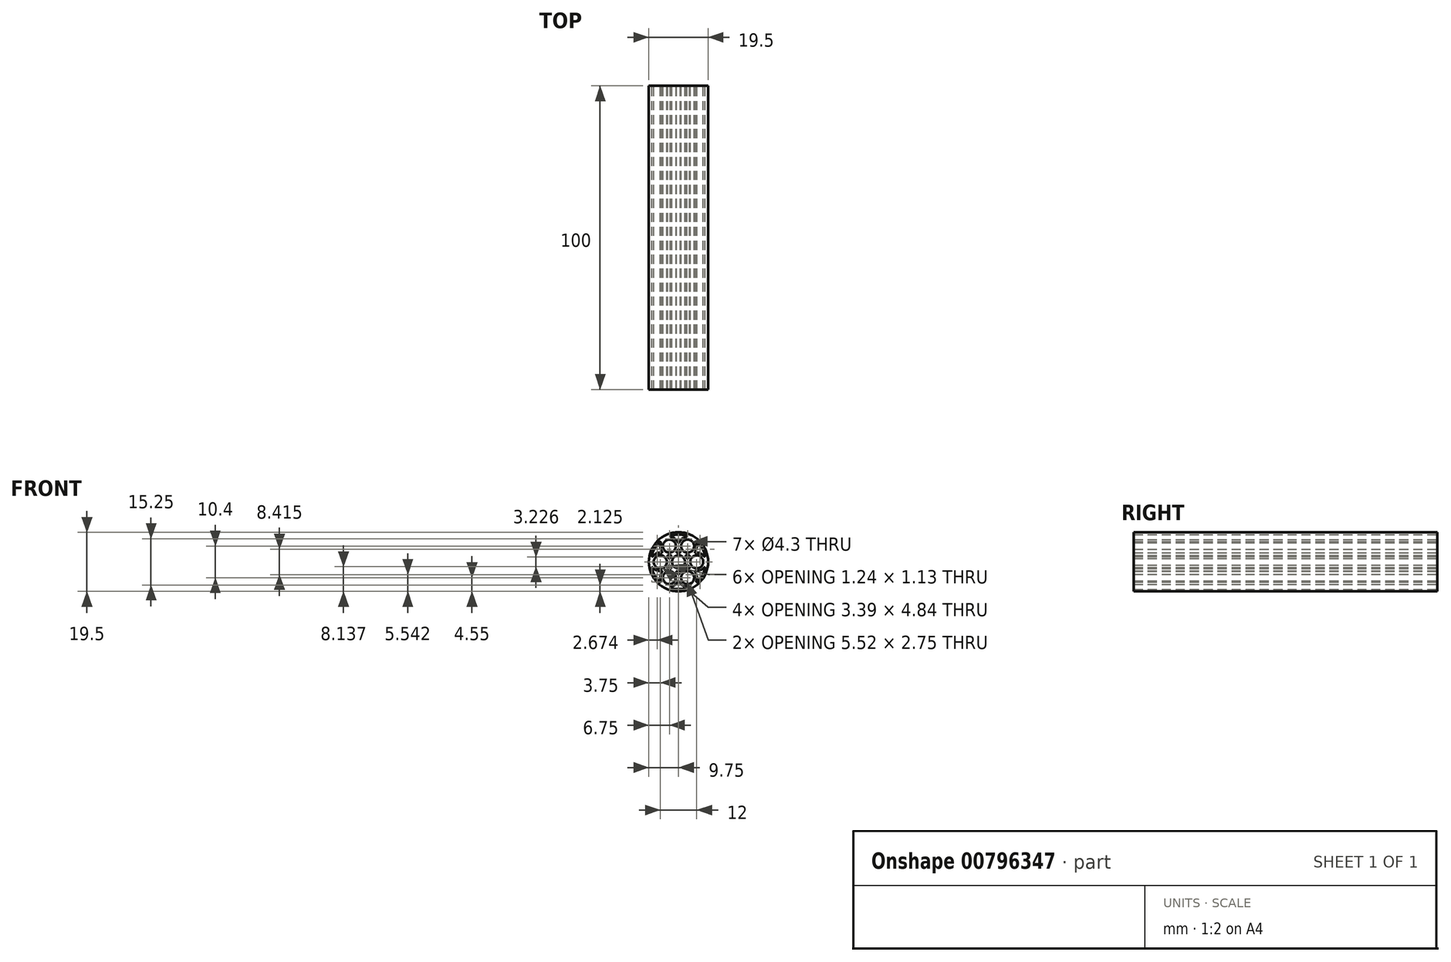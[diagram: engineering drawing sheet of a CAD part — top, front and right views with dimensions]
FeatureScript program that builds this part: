
annotation { "Feature Type Name" : "Feature", "Feature Type Description" : "" }
export const myFeature = defineFeature(function(context is Context, id is Id, definition is map)
    precondition{}
    {
        {
            var Q0;
            Q0=qCreatedBy(makeId("Front.planeOp"),FACE);
            var sketch = newSketch(context, id + "F0", { "sketchPlane" : qUnion([Q0])});
            skArc(sketch, "E0", {"start": v(2.82, 1.17) * mm, "mid": v(2.64, 1.53) * mm, "end": v(2.42, 1.86) * mm});
            skArc(sketch, "E1.1.0.0", {"start": v(3.18, -1.17) * mm, "mid": v(3.36, -1.53) * mm, "end": v(3.58, -1.86) * mm});
            skArc(sketch, "E1.2.0.0", {"start": v(9.18, -1.17) * mm, "mid": v(9.36, -1.53) * mm, "end": v(9.58, -1.86) * mm});
            skLineSegment(sketch, "E1.direction1", {"start": v(0, 0) * mm, "end": v(6, 0) * mm, "construction": true});
            skArc(sketch, "E2.trimOffspring", {"start": v(8.82, 1.17) * mm, "mid": v(8.64, 1.53) * mm, "end": v(8.42, 1.86) * mm});
            skArc(sketch, "E3", {"start": v(2.6, 2.18) * mm, "mid": v(3, 2.15) * mm, "end": v(3.4, 2.18) * mm});
            skArc(sketch, "E4.1.0.0", {"start": v(8.6, 2.18) * mm, "mid": v(9, 2.15) * mm, "end": v(9.4, 2.18) * mm});
            skLineSegment(sketch, "E4.direction1", {"start": v(3, 5.2) * mm, "end": v(9, 5.2) * mm, "construction": true});
            skArc(sketch, "E5.0.1.0", {"start": v(6.58, -3.34) * mm, "mid": v(6.36, -3.67) * mm, "end": v(6.18, -4.03) * mm});
            skArc(sketch, "E5.0.1.1", {"start": v(3.4, -2.18) * mm, "mid": v(3, -2.15) * mm, "end": v(2.6, -2.18) * mm});
            skLineSegment(sketch, "E5.direction1", {"start": v(9, 5.2) * mm, "end": v(34, 5.2) * mm, "construction": true});
            skLineSegment(sketch, "E5.direction2", {"start": v(9, 5.2) * mm, "end": v(9, -5.2) * mm, "construction": true});
            skArc(sketch, "E6.trimOffspring", {"start": v(0.4, 3.02) * mm, "mid": v(-1.16, 2.82) * mm, "end": v(-2.41, 1.86) * mm});
            skArc(sketch, "E7.trimOffspring", {"start": v(5.42, 3.34) * mm, "mid": v(5.64, 3.67) * mm, "end": v(5.82, 4.03) * mm});
            skArc(sketch, "E8.trimOffspring", {"start": v(3.58, 1.86) * mm, "mid": v(3.36, 1.53) * mm, "end": v(3.18, 1.17) * mm});
            skArc(sketch, "E9.trimOffspring", {"start": v(6.4, 3.02) * mm, "mid": v(6, 3.05) * mm, "end": v(5.6, 3.02) * mm});
            skArc(sketch, "E10.trimOffspring", {"start": v(9.58, 1.86) * mm, "mid": v(9.36, 1.53) * mm, "end": v(9.18, 1.17) * mm});
            skArc(sketch, "E11.trimOffspring", {"start": v(11.42, 3.34) * mm, "mid": v(12.02, 4.8) * mm, "end": v(11.82, 6.35) * mm});
            skArc(sketch, "E12.trimOffspring", {"start": v(8.42, -1.86) * mm, "mid": v(8.64, -1.53) * mm, "end": v(8.82, -1.17) * mm});
            skArc(sketch, "E13.trimOffspring", {"start": v(5.6, -3.02) * mm, "mid": v(6, -3.05) * mm, "end": v(6.4, -3.02) * mm});
            skArc(sketch, "E14.trimOffspring", {"start": v(2.42, -1.86) * mm, "mid": v(2.64, -1.53) * mm, "end": v(2.82, -1.17) * mm});
            skArc(sketch, "E15.trimOffspring", {"start": v(0.58, -3.34) * mm, "mid": v(-0.02, -4.8) * mm, "end": v(0.18, -6.35) * mm});
            skArc(sketch, "E16.trimOffspring", {"start": v(6.18, 4.03) * mm, "mid": v(6.36, 3.67) * mm, "end": v(6.58, 3.34) * mm});
            skArc(sketch, "E17.trimOffspring", {"start": v(5.82, 6.37) * mm, "mid": v(4.86, 7.62) * mm, "end": v(3.41, 8.22) * mm});
            skCircle(sketch, "E18", {"center": v(0, 0) * mm, "radius": 2.15 * mm});
            skCircle(sketch, "E19", {"center": v(3, 5.2) * mm, "radius": 2.15 * mm});
            skCircle(sketch, "E20", {"center": v(9, 5.2) * mm, "radius": 2.15 * mm});
            skCircle(sketch, "E21", {"center": v(12, 0) * mm, "radius": 2.15 * mm});
            skCircle(sketch, "E22", {"center": v(6, 0) * mm, "radius": 2.15 * mm});
            skCircle(sketch, "E23", {"center": v(3, -5.2) * mm, "radius": 2.15 * mm});
            skCircle(sketch, "E24", {"center": v(9, -5.2) * mm, "radius": 2.15 * mm});
            skArc(sketch, "E25.trimOffspring", {"start": v(5.82, -4.03) * mm, "mid": v(5.64, -3.67) * mm, "end": v(5.42, -3.34) * mm});
            skArc(sketch, "E26.trimOffspring", {"start": v(6.18, -6.37) * mm, "mid": v(7.14, -7.62) * mm, "end": v(8.59, -8.22) * mm});
            skPoint(sketch, "E27.visualSharp", {"position": v(6, 5.75) * mm});
            skArc(sketch, "E27.filletArc", {"start": v(5.82, 6.37) * mm, "mid": v(6, 6.25) * mm, "end": v(6.18, 6.37) * mm});
            skPoint(sketch, "E28.visualSharp", {"position": v(6, 4.65) * mm});
            skArc(sketch, "E28.filletArc", {"start": v(6.18, 4.03) * mm, "mid": v(6, 4.15) * mm, "end": v(5.82, 4.03) * mm});
            skPoint(sketch, "E29.visualSharp", {"position": v(4.97, 2.87) * mm});
            skArc(sketch, "E29.filletArc", {"start": v(5.42, 3.34) * mm, "mid": v(5.4, 3.12) * mm, "end": v(5.6, 3.02) * mm});
            skPoint(sketch, "E30.visualSharp", {"position": v(7.03, 2.87) * mm});
            skArc(sketch, "E30.filletArc", {"start": v(6.4, 3.02) * mm, "mid": v(6.6, 3.12) * mm, "end": v(6.58, 3.34) * mm});
            skPoint(sketch, "E31.visualSharp", {"position": v(7.97, 2.33) * mm});
            skArc(sketch, "E31.filletArc", {"start": v(8.6, 2.18) * mm, "mid": v(8.4, 2.08) * mm, "end": v(8.42, 1.86) * mm});
            skPoint(sketch, "E32.visualSharp", {"position": v(10.03, 2.33) * mm});
            skArc(sketch, "E32.filletArc", {"start": v(9.58, 1.86) * mm, "mid": v(9.6, 2.08) * mm, "end": v(9.4, 2.18) * mm});
            skPoint(sketch, "E33.visualSharp", {"position": v(9, 0.55) * mm});
            skArc(sketch, "E33.filletArc", {"start": v(8.82, 1.17) * mm, "mid": v(9, 1.05) * mm, "end": v(9.18, 1.17) * mm});
            skPoint(sketch, "E34.visualSharp", {"position": v(9, -0.55) * mm});
            skArc(sketch, "E34.filletArc", {"start": v(9.18, -1.17) * mm, "mid": v(9, -1.05) * mm, "end": v(8.82, -1.17) * mm});
            skPoint(sketch, "E35.visualSharp", {"position": v(7.97, -2.33) * mm});
            skArc(sketch, "E35.filletArc", {"start": v(8.42, -1.86) * mm, "mid": v(8.4, -2.08) * mm, "end": v(8.6, -2.18) * mm});
            skPoint(sketch, "E36.visualSharp", {"position": v(10.97, 2.87) * mm});
            skArc(sketch, "E36.filletArc", {"start": v(11.42, 3.34) * mm, "mid": v(11.4, 3.12) * mm, "end": v(11.6, 3.02) * mm});
            skPoint(sketch, "E37.visualSharp", {"position": v(3, -0.55) * mm});
            skArc(sketch, "E37.filletArc", {"start": v(3.18, -1.17) * mm, "mid": v(3, -1.05) * mm, "end": v(2.82, -1.17) * mm});
            skPoint(sketch, "E38.visualSharp", {"position": v(1.97, -2.33) * mm});
            skArc(sketch, "E38.filletArc", {"start": v(2.42, -1.86) * mm, "mid": v(2.4, -2.08) * mm, "end": v(2.6, -2.18) * mm});
            skPoint(sketch, "E39.visualSharp", {"position": v(4.03, -2.33) * mm});
            skArc(sketch, "E39.filletArc", {"start": v(3.4, -2.18) * mm, "mid": v(3.6, -2.08) * mm, "end": v(3.58, -1.86) * mm});
            skPoint(sketch, "E40.visualSharp", {"position": v(4.97, -2.87) * mm});
            skArc(sketch, "E40.filletArc", {"start": v(5.6, -3.02) * mm, "mid": v(5.4, -3.12) * mm, "end": v(5.42, -3.34) * mm});
            skPoint(sketch, "E41.visualSharp", {"position": v(7.03, -2.87) * mm});
            skArc(sketch, "E41.filletArc", {"start": v(6.58, -3.34) * mm, "mid": v(6.6, -3.12) * mm, "end": v(6.4, -3.02) * mm});
            skPoint(sketch, "E42.visualSharp", {"position": v(6, -4.65) * mm});
            skArc(sketch, "E42.filletArc", {"start": v(5.82, -4.03) * mm, "mid": v(6, -4.15) * mm, "end": v(6.18, -4.03) * mm});
            skPoint(sketch, "E43.visualSharp", {"position": v(1.03, -2.87) * mm});
            skArc(sketch, "E43.filletArc", {"start": v(0.58, -3.34) * mm, "mid": v(0.6, -3.12) * mm, "end": v(0.4, -3.02) * mm});
            skPoint(sketch, "E44.visualSharp", {"position": v(1.03, 2.87) * mm});
            skArc(sketch, "E44.filletArc", {"start": v(0.4, 3.02) * mm, "mid": v(0.6, 3.12) * mm, "end": v(0.58, 3.34) * mm});
            skPoint(sketch, "E45.visualSharp", {"position": v(1.97, 2.33) * mm});
            skArc(sketch, "E45.filletArc", {"start": v(2.6, 2.18) * mm, "mid": v(2.4, 2.08) * mm, "end": v(2.42, 1.86) * mm});
            skPoint(sketch, "E46.visualSharp", {"position": v(4.03, 2.33) * mm});
            skArc(sketch, "E46.filletArc", {"start": v(3.58, 1.86) * mm, "mid": v(3.6, 2.08) * mm, "end": v(3.4, 2.18) * mm});
            skPoint(sketch, "E47.visualSharp", {"position": v(3, 0.55) * mm});
            skArc(sketch, "E47.filletArc", {"start": v(2.82, 1.17) * mm, "mid": v(3, 1.05) * mm, "end": v(3.18, 1.17) * mm});
            skPoint(sketch, "E48.visualSharp", {"position": v(6, -5.75) * mm});
            skArc(sketch, "E48.filletArc", {"start": v(6.18, -6.37) * mm, "mid": v(6, -6.25) * mm, "end": v(5.82, -6.37) * mm});
            skArc(sketch, "E49.trimOffspring", {"start": v(11.6, -3.02) * mm, "mid": v(13.16, -2.82) * mm, "end": v(14.41, -1.86) * mm});
            skArc(sketch, "E50.trimOffspring", {"start": v(9.4, -2.18) * mm, "mid": v(9, -2.15) * mm, "end": v(8.6, -2.18) * mm});
            skPoint(sketch, "E51.visualSharp", {"position": v(10.03, -2.33) * mm});
            skArc(sketch, "E51.filletArc", {"start": v(9.4, -2.18) * mm, "mid": v(9.6, -2.08) * mm, "end": v(9.58, -1.86) * mm});
            skPoint(sketch, "E52.visualSharp", {"position": v(10.97, -2.87) * mm});
            skArc(sketch, "E52.filletArc", {"start": v(11.6, -3.02) * mm, "mid": v(11.4, -3.12) * mm, "end": v(11.42, -3.34) * mm});
            skArc(sketch, "E53", {"start": v(-0.15, 6.58) * mm, "mid": v(-1.8, 4.5) * mm, "end": v(-2.77, 2.03) * mm});
            skCircle(sketch, "E54", {"center": v(6, 0) * mm, "radius": 9.75 * mm});
            skArc(sketch, "E55.trimOffspring", {"start": v(0.18, 6.35) * mm, "mid": v(-0.02, 4.8) * mm, "end": v(0.58, 3.34) * mm});
            skArc(sketch, "E56.trimOffspring", {"start": v(8.59, 8.22) * mm, "mid": v(7.14, 7.62) * mm, "end": v(6.18, 6.37) * mm});
            skArc(sketch, "E57.trimOffspring", {"start": v(8.62, 8.61) * mm, "mid": v(6, 9) * mm, "end": v(3.38, 8.61) * mm});
            skArc(sketch, "E58.trimOffspring", {"start": v(14.41, 1.86) * mm, "mid": v(13.16, 2.82) * mm, "end": v(11.6, 3.02) * mm});
            skArc(sketch, "E59.trimOffspring", {"start": v(14.77, 2.03) * mm, "mid": v(13.8, 4.5) * mm, "end": v(12.15, 6.58) * mm});
            skArc(sketch, "E60.trimOffspring", {"start": v(12.15, -6.58) * mm, "mid": v(13.8, -4.5) * mm, "end": v(14.77, -2.03) * mm});
            skArc(sketch, "E61.trimOffspring", {"start": v(11.82, -6.35) * mm, "mid": v(12.02, -4.8) * mm, "end": v(11.42, -3.34) * mm});
            skArc(sketch, "E62.trimOffspring", {"start": v(3.41, -8.22) * mm, "mid": v(4.86, -7.62) * mm, "end": v(5.82, -6.37) * mm});
            skArc(sketch, "E63.trimOffspring", {"start": v(3.38, -8.61) * mm, "mid": v(6, -9) * mm, "end": v(8.62, -8.61) * mm});
            skArc(sketch, "E64.trimOffspring", {"start": v(-2.77, -2.03) * mm, "mid": v(-1.8, -4.5) * mm, "end": v(-0.15, -6.58) * mm});
            skArc(sketch, "E65.trimOffspring", {"start": v(-2.41, -1.86) * mm, "mid": v(-1.16, -2.82) * mm, "end": v(0.4, -3.02) * mm});
            skPoint(sketch, "E66.visualSharp", {"position": v(11.09, 7.43) * mm});
            skArc(sketch, "E66.filletArc", {"start": v(12.15, 6.58) * mm, "mid": v(11.9, 6.6) * mm, "end": v(11.82, 6.35) * mm});
            skPoint(sketch, "E67.visualSharp", {"position": v(14.97, 0.67) * mm});
            skArc(sketch, "E67.filletArc", {"start": v(14.41, 1.86) * mm, "mid": v(14.66, 1.8) * mm, "end": v(14.77, 2.03) * mm});
            skPoint(sketch, "E68.visualSharp", {"position": v(14.97, -0.67) * mm});
            skArc(sketch, "E68.filletArc", {"start": v(14.77, -2.03) * mm, "mid": v(14.66, -1.8) * mm, "end": v(14.41, -1.86) * mm});
            skPoint(sketch, "E69.visualSharp", {"position": v(11.09, -7.43) * mm});
            skArc(sketch, "E69.filletArc", {"start": v(11.82, -6.35) * mm, "mid": v(11.9, -6.6) * mm, "end": v(12.15, -6.58) * mm});
            skPoint(sketch, "E70.visualSharp", {"position": v(9.88, -8.12) * mm});
            skArc(sketch, "E70.filletArc", {"start": v(8.62, -8.61) * mm, "mid": v(8.76, -8.4) * mm, "end": v(8.59, -8.22) * mm});
            skPoint(sketch, "E71.visualSharp", {"position": v(2.12, -8.12) * mm});
            skArc(sketch, "E71.filletArc", {"start": v(3.41, -8.22) * mm, "mid": v(3.24, -8.4) * mm, "end": v(3.38, -8.61) * mm});
            skPoint(sketch, "E72.visualSharp", {"position": v(0.91, -7.43) * mm});
            skArc(sketch, "E72.filletArc", {"start": v(-0.15, -6.58) * mm, "mid": v(0.1, -6.6) * mm, "end": v(0.18, -6.35) * mm});
            skPoint(sketch, "E73.visualSharp", {"position": v(-2.97, -0.67) * mm});
            skArc(sketch, "E73.filletArc", {"start": v(-2.41, -1.86) * mm, "mid": v(-2.66, -1.8) * mm, "end": v(-2.77, -2.03) * mm});
            skPoint(sketch, "E74.visualSharp", {"position": v(-2.97, 0.67) * mm});
            skArc(sketch, "E74.filletArc", {"start": v(-2.77, 2.03) * mm, "mid": v(-2.66, 1.8) * mm, "end": v(-2.41, 1.86) * mm});
            skPoint(sketch, "E75.visualSharp", {"position": v(0.91, 7.43) * mm});
            skArc(sketch, "E75.filletArc", {"start": v(0.18, 6.35) * mm, "mid": v(0.1, 6.6) * mm, "end": v(-0.15, 6.58) * mm});
            skPoint(sketch, "E76.visualSharp", {"position": v(2.12, 8.12) * mm});
            skArc(sketch, "E76.filletArc", {"start": v(3.38, 8.61) * mm, "mid": v(3.24, 8.4) * mm, "end": v(3.41, 8.22) * mm});
            skPoint(sketch, "E77.visualSharp", {"position": v(9.88, 8.12) * mm});
            skArc(sketch, "E77.filletArc", {"start": v(8.59, 8.22) * mm, "mid": v(8.76, 8.4) * mm, "end": v(8.62, 8.61) * mm});
            skSolve(sketch);
        }
        {
            var Q0;
            Q0 = qSketchRegion(id + "F0", true);
            extrude(context, id + "F1", {"entities" : qUnion([Q0]), "depth" : 100 * mm, "offsetDistance" : 25 * mm});
        }
    });
